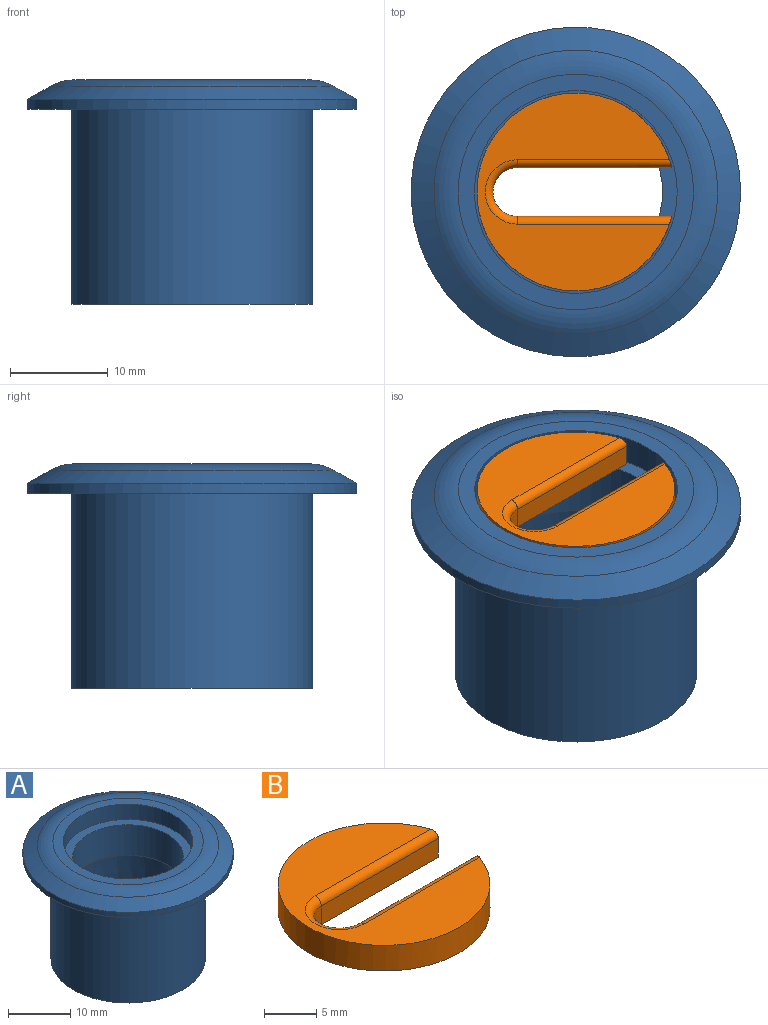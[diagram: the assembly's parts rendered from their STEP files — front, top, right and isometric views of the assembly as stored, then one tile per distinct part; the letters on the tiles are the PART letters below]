
ASSEMBLY  parts=2 mates=1
PART A: 11 faces, bbox 33.8x33.8x23 mm
  f0: plane 24.14x24.14mm, normal (0,0,1), area 118.1mm2, adj f1,f10
  f1: cylinder r=10.4mm len=20.8mm, axis (0,0,1), area 196mm2, adj f0,f2
  f2: plane 20.8x20.8mm, normal (0,0,1), area 90.9mm2, adj f1,f3
  f3: cylinder r=8.9mm len=17.8mm, axis (0,0,1), area 335.5mm2, adj f2,f4
  f4: cone r=8.9mm half-angle=6.1deg, axis (0,0,-1), area 853.7mm2, adj f3,f5
  f5: plane 24.8x24.8mm, normal (0,0,-1), area 143.3mm2, adj f4,f6
  f6: cylinder r=12.4mm len=24.8mm, axis (0,0,1), area 1558.2mm2, adj f5,f7
  f7: plane 33.8x33.8mm, normal (0,0,-1), area 414.2mm2, adj f6,f8
  f8: cylinder r=16.9mm len=33.8mm, axis (0,0,1), area 106.2mm2, adj f7,f9
  f9: cone r=14.55mm half-angle=60.3deg, axis (0,0,-1), area 267.1mm2, adj f8,f10
  f10: torus R=12.07mm, axis (0,0,1), area 217.6mm2, adj f0,f9
PART B: 9 faces, bbox 20x20.3x3 mm
  f0: plane 15.84x2.2mm, normal (0,-1,0), area 34.8mm2, adj f1,f3,f5,f6
  f1: cylinder r=10.15mm len=20.3mm, axis (0,0,-1), area 175.9mm2, adj f0,f2,f4,f5,f6,f8
  f2: plane 15.84x2.2mm, normal (0,1,0), area 34.8mm2, adj f1,f3,f5,f8
  f3: cylinder r=2.5mm len=5mm, axis (0,0,-1), area 17.3mm2, adj f0,f2,f5,f7
  f4: plane 20.3x19.75mm, normal (0,0,1), area 201.2mm2, adj f1,f6,f7,f8
  f5: plane 20.3x19.99mm, normal (0,0,-1), area 233.6mm2, adj f0,f1,f2,f3
  f6: cylinder r=0.8mm len=15.84mm, axis (-1,0,0), area 19.8mm2, adj f0,f1,f4,f7
  f7: torus R=3.3mm, axis (0,0,1), area 11mm2, adj f3,f4,f6,f8
  f8: cylinder r=0.8mm len=15.84mm, axis (1,0,0), area 19.8mm2, adj f1,f2,f4,f7
PLACE A at identity
PLACE B t=(0,0,20)mm
MATE fastened B.f1 <-> A.f1  axis (0,0,-1) through (0,0,20)mm
